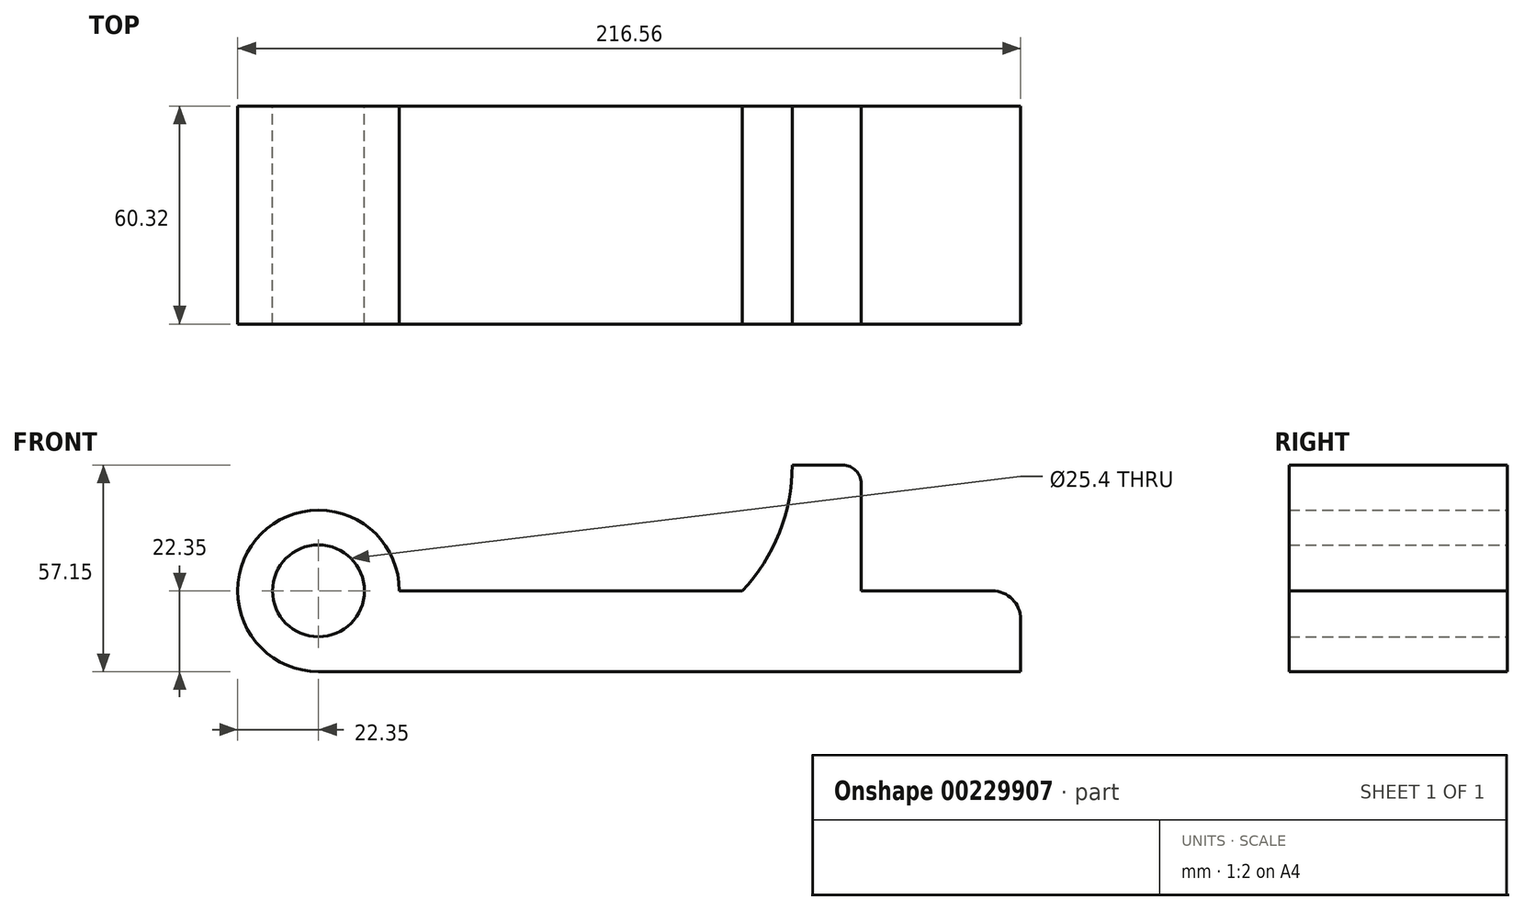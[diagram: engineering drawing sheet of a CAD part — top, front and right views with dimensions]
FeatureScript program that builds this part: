
annotation { "Feature Type Name" : "Feature", "Feature Type Description" : "" }
export const myFeature = defineFeature(function(context is Context, id is Id, definition is map)
    precondition{}
    {
        {
            var Q0;
            Q0=qCreatedBy(makeId("Front.planeOp"),FACE);
            var sketch = newSketch(context, id + "F0", { "sketchPlane" : qUnion([Q0])});
            skCircle(sketch, "E0", {"center": v(0, 0) * mm, "radius": 12.7 * mm});
            skArc(sketch, "E1", {"start": v(22.35, 0) * mm, "mid": v(-15.8, 15.8) * mm, "end": v(0, -22.35) * mm});
            skLineSegment(sketch, "E2", {"start": v(0, -22.35) * mm, "end": v(194.2, -22.35) * mm});
            skPoint(sketch, "E3", {"position": v(-22.35, 0) * mm});
            skLineSegment(sketch, "E4", {"start": v(150.09, 0) * mm, "end": v(150.09, 29.72) * mm});
            skLineSegment(sketch, "E5", {"start": v(145, 34.8) * mm, "end": v(131.04, 34.8) * mm});
            skPoint(sketch, "E6.visualSharp", {"position": v(150.09, 34.8) * mm});
            skArc(sketch, "E6.filletArc", {"start": v(150.09, 29.72) * mm, "mid": v(148.6, 33.31) * mm, "end": v(145, 34.8) * mm});
            skLineSegment(sketch, "E7", {"start": v(150.09, 0) * mm, "end": v(186.33, 0) * mm});
            skLineSegment(sketch, "E8", {"start": v(194.2, -7.87) * mm, "end": v(194.2, -22.35) * mm});
            skPoint(sketch, "E9.orphan", {"position": v(150.09, -22.35) * mm});
            skPoint(sketch, "E10.visualSharp", {"position": v(194.2, 0) * mm});
            skArc(sketch, "E10.filletArc", {"start": v(194.2, -7.87) * mm, "mid": v(191.9, -2.3) * mm, "end": v(186.33, 0) * mm});
            skArc(sketch, "E11", {"start": v(117.25, 0) * mm, "mid": v(127.46, 16.08) * mm, "end": v(131.04, 34.8) * mm});
            skLineSegment(sketch, "E12.trimOffspring", {"start": v(22.35, 0) * mm, "end": v(117.25, 0) * mm});
            skSolve(sketch);
        }
        {
            var Q0;
            Q0 = qSketchRegion(id + "F0", true);
            extrude(context, id + "F1", {"entities" : qUnion([Q0]), "endBound" : BoundingType.SYMMETRIC, "depth" : 60.32 * mm});
        }
    });
